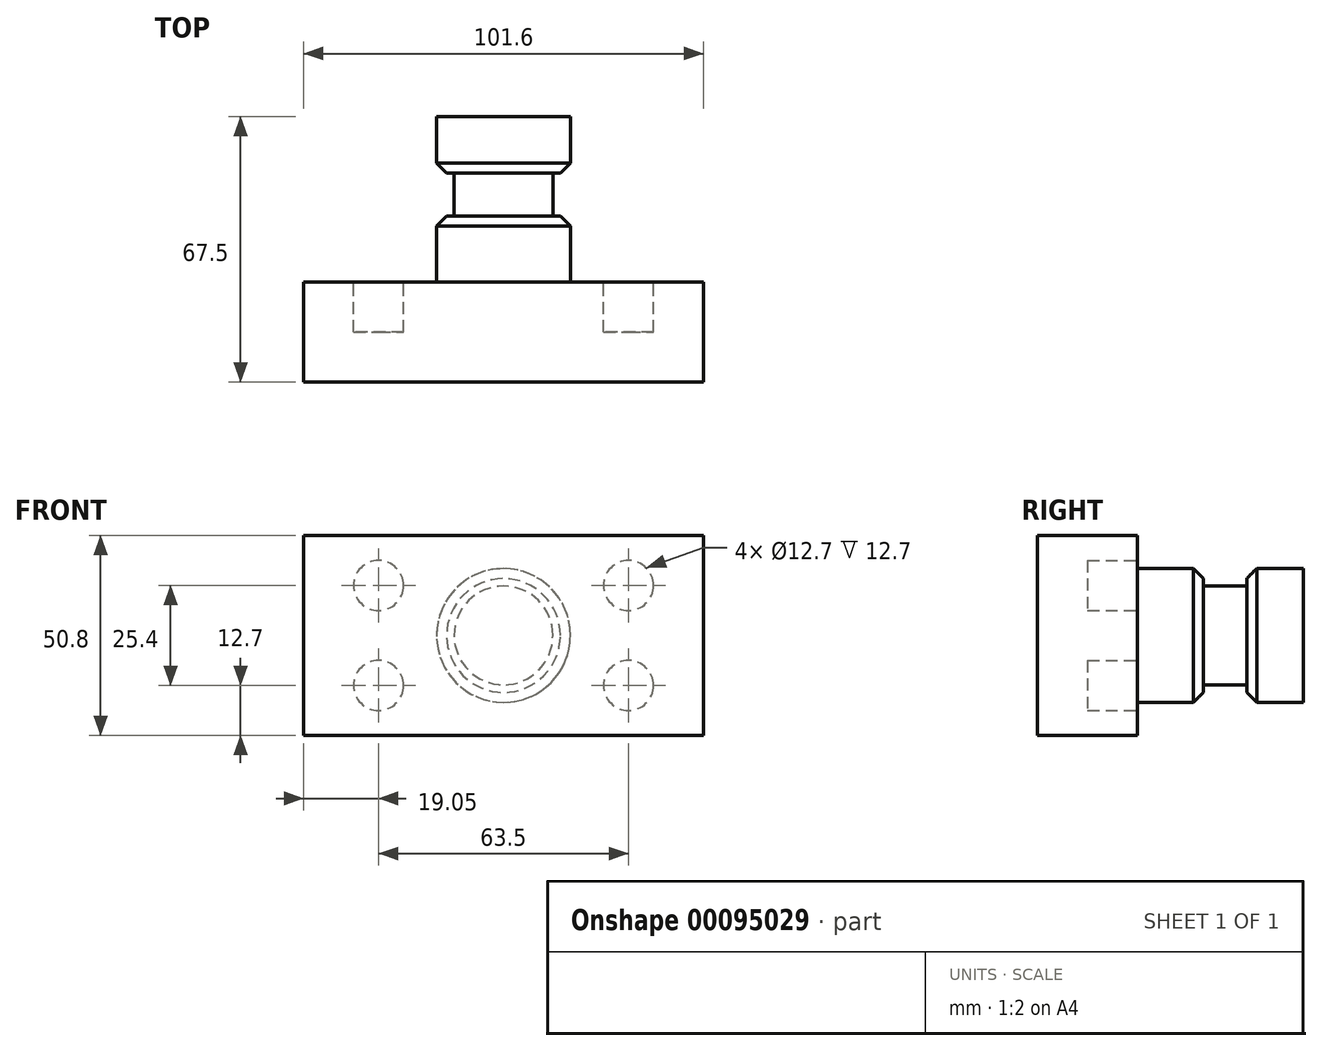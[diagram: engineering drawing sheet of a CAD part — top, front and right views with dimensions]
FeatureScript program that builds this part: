
annotation { "Feature Type Name" : "Feature", "Feature Type Description" : "" }
export const myFeature = defineFeature(function(context is Context, id is Id, definition is map)
    precondition{}
    {
        {
            var Q0;
            Q0=qCreatedBy(makeId("Front.planeOp"),FACE);
            var sketch = newSketch(context, id + "F0", { "sketchPlane" : qUnion([Q0])});
            skLineSegment(sketch, "E0.bottom", {"start": v(50.8, 25.4) * mm, "end": v(-50.8, 25.4) * mm});
            skLineSegment(sketch, "E0.top", {"start": v(50.8, -25.4) * mm, "end": v(-50.8, -25.4) * mm});
            skLineSegment(sketch, "E0.left", {"start": v(50.8, 25.4) * mm, "end": v(50.8, -25.4) * mm});
            skLineSegment(sketch, "E0.right", {"start": v(-50.8, 25.4) * mm, "end": v(-50.8, -25.4) * mm});
            skPoint(sketch, "E0.middle", {"position": v(0, 0) * mm});
            skSolve(sketch);
        }
        {
            var Q0;
            Q0 = qSketchRegion(id + "F0", true);
            extrude(context, id + "F1", {"entities" : qUnion([Q0]), "depth" : 25.4 * mm});
        }
        {
            var Q0;
            Q0=makeQuery(id+"F1.opExtrude","CAP_FACE",FACE,{"disambiguationData":[OSD([sQuery(id+"F0.wireOp",EDGE,"E0.bottom"),sQuery(id+"F0.wireOp",EDGE,"E0.top"),sQuery(id+"F0.wireOp",EDGE,"E0.left"),sQuery(id+"F0.wireOp",EDGE,"E0.right")])],"isStart":true});
            var sketch = newSketch(context, id + "F2", { "sketchPlane" : qUnion([Q0])});
            skCircle(sketch, "E1", {"center": v(-31.75, 12.7) * mm, "radius": 6.35 * mm});
            skCircle(sketch, "E2", {"center": v(31.75, 12.7) * mm, "radius": 6.35 * mm});
            skCircle(sketch, "E3", {"center": v(31.75, -12.7) * mm, "radius": 6.35 * mm});
            skCircle(sketch, "E4", {"center": v(-31.75, -12.7) * mm, "radius": 6.35 * mm});
            skSolve(sketch);
        }
        {
            var Q0;
            Q0=makeQuery(id+"F2.imprint","IMPRINT",FACE,{"disambiguationData":[TD([[makeQuery(id+"F2.imprint","IMPRINT",EDGE,{"derivedFrom":sQuery(id+"F2.wireOp",EDGE,"E3")}),1.0]])]});
            var Q1;
            Q1=makeQuery(id+"F2.imprint","IMPRINT",FACE,{"disambiguationData":[TD([[makeQuery(id+"F2.imprint","IMPRINT",EDGE,{"derivedFrom":sQuery(id+"F2.wireOp",EDGE,"E1")}),1.0]])]});
            var Q2;
            Q2=makeQuery(id+"F2.imprint","IMPRINT",FACE,{"disambiguationData":[TD([[makeQuery(id+"F2.imprint","IMPRINT",EDGE,{"derivedFrom":sQuery(id+"F2.wireOp",EDGE,"E4")}),1.0]])]});
            var Q3;
            Q3=makeQuery(id+"F2.imprint","IMPRINT",FACE,{"disambiguationData":[TD([[makeQuery(id+"F2.imprint","IMPRINT",EDGE,{"derivedFrom":sQuery(id+"F2.wireOp",EDGE,"E2")}),1.0]])]});
            var Q4;
            Q4=sQuery(id+"F2.wireOp",EDGE,"E3");
            var Q5;
            Q5=sQuery(id+"F2.wireOp",EDGE,"E2");
            var Q6;
            Q6=sQuery(id+"F2.wireOp",EDGE,"E1");
            var Q7;
            Q7=sQuery(id+"F2.wireOp",EDGE,"E4");
            extrude(context, id + "F3", {"entities" : qUnion([Q0, Q1, Q2, Q3]), "operationType" : NewBodyOperationType.REMOVE, "surfaceEntities" : qUnion([Q4, Q5, Q6, Q7]), "oppositeDirection" : true, "depth" : 12.7 * mm});
        }
        {
            var Q0;
            Q0=qCreatedBy(makeId("Top.planeOp"),FACE);
            var sketch = newSketch(context, id + "F4", { "sketchPlane" : qUnion([Q0])});
            skLineSegment(sketch, "E5", {"start": v(0, 0) * mm, "end": v(0, 42.1) * mm});
            skLineSegment(sketch, "E6", {"start": v(0, 42.1) * mm, "end": v(-17, 42.1) * mm});
            skLineSegment(sketch, "E7", {"start": v(-17, 42.1) * mm, "end": v(-17, 27.72) * mm});
            skLineSegment(sketch, "E8", {"start": v(-17, 27.72) * mm, "end": v(-12.55, 27.72) * mm});
            skLineSegment(sketch, "E9", {"start": v(-12.55, 27.72) * mm, "end": v(-12.55, 16.73) * mm});
            skLineSegment(sketch, "E10", {"start": v(-12.55, 16.73) * mm, "end": v(-17, 16.73) * mm});
            skLineSegment(sketch, "E11", {"start": v(-17, 16.73) * mm, "end": v(-17, 0) * mm});
            skLineSegment(sketch, "E12", {"start": v(-17, 0) * mm, "end": v(0, 0) * mm});
            skSolve(sketch);
        }
        {
            var Q0;
            Q0=makeQuery(id+"F4.imprint","IMPRINT",FACE,{"disambiguationData":[TD([[makeQuery(id+"F4.imprint","IMPRINT",EDGE,{"derivedFrom":sQuery(id+"F4.wireOp",EDGE,"E5")}),1.0]])]});
            var Q1;
            Q1=sQuery(id+"F4.wireOp",EDGE,"E5");
            revolve(context, id + "F5", {"operationType" : NewBodyOperationType.ADD, "entities" : qUnion([Q0]), "axis" : qUnion([Q1]), "revolveType" : RevolveType.FULL});
        }
        {
            var Q0;
            Q0=makeQuery(id+"F5.opRevolve","SWEPT_EDGE",EDGE,{"disambiguationData":[OSD([sQuery(id+"F4.wireOp",EDGE,"E10"),sQuery(id+"F4.wireOp",EDGE,"E11")])]});
            var Q1;
            Q1=makeQuery(id+"F5.opRevolve","SWEPT_EDGE",EDGE,{"disambiguationData":[OSD([sQuery(id+"F4.wireOp",EDGE,"E7"),sQuery(id+"F4.wireOp",EDGE,"E8")])]});
            chamfer(context, id + "F6", {"entities" : qUnion([Q0, Q1]), "width" : 2.54 * mm, "tangentPropagation" : true});
        }
    });
